# Revit family: Domotics-DomesticRanges-GEWISS-CHORUS_DATA-CONNECTOR_PHONIC
name_source: partatom
category: Apparecchi elettrici
revit_build: Autodesk Revit 2016 (Build: 20161004_0715(x64)
units: mm (PartAtom-declared; Revit-internal decimal feet)

## family parameters
Condiviso = Sì
Host = Superficie
Mantenere orientamento annotazione = Sì
Punto di calcolo locali = Sì
Quota connettore circolare = Usa diametro
Taglio con vuoti quando caricato = No
Tipo di parte = Normale

## types (3) — shared parameters
Catalogue = DOMOTICS
Catalogue Range = CHORUS - SERIE CIVILE
Category = Connector
Description. = Connector
Description: = Phonic circuits
Electrocod = 3720
IDF = 0c0c5c58-57c8-43a8-9b5b-dbd5238ef18e
IDT = 1977e26f-af39-45f8-969d-aeddd281689b
Immagine tipo = GW14454.jpg
No. Chorus modules: = 1
Produttore = GEWISS S.p.A.
Prospetto di default = 1219 mm
SEO = Socket outlet
Standard; = DIN 41529
Technical sheet = https://www.gewiss.com
Tipo_ = CONNETTORE CIRCUITI FONICI : titanio
URL = https://www.gewiss.com
Version file RFA = 19.0
struttura = Default

## per-type parameters (varying)
| type | Colour | Descrizione | EAN code | Modello |
| GW12454 - CONNECTOR PHONIC CIRCUITS 1M CHORUS B | Black | CONNECTOR PHONIC CIRCUITS 1M CHORUS B | 8011564269187 | GW12454 |
| GW14454 - CONNECTOR, PHONIC CIRCUITS 1M TITANIUM | Titanium | CONNECTOR, PHONIC CIRCUITS 1M TITANIUM | 8011564265196 | GW14454 |
| GW10454 - CONNECTOR PHONIC CIRCUITS 1M WHITE | White | CONNECTOR PHONIC CIRCUITS 1M WHITE | 8011564259515 | GW10454 |

## geometry (parser evidence)
native form markers: Sweep x1
no freeform markers — native parametric forms only
